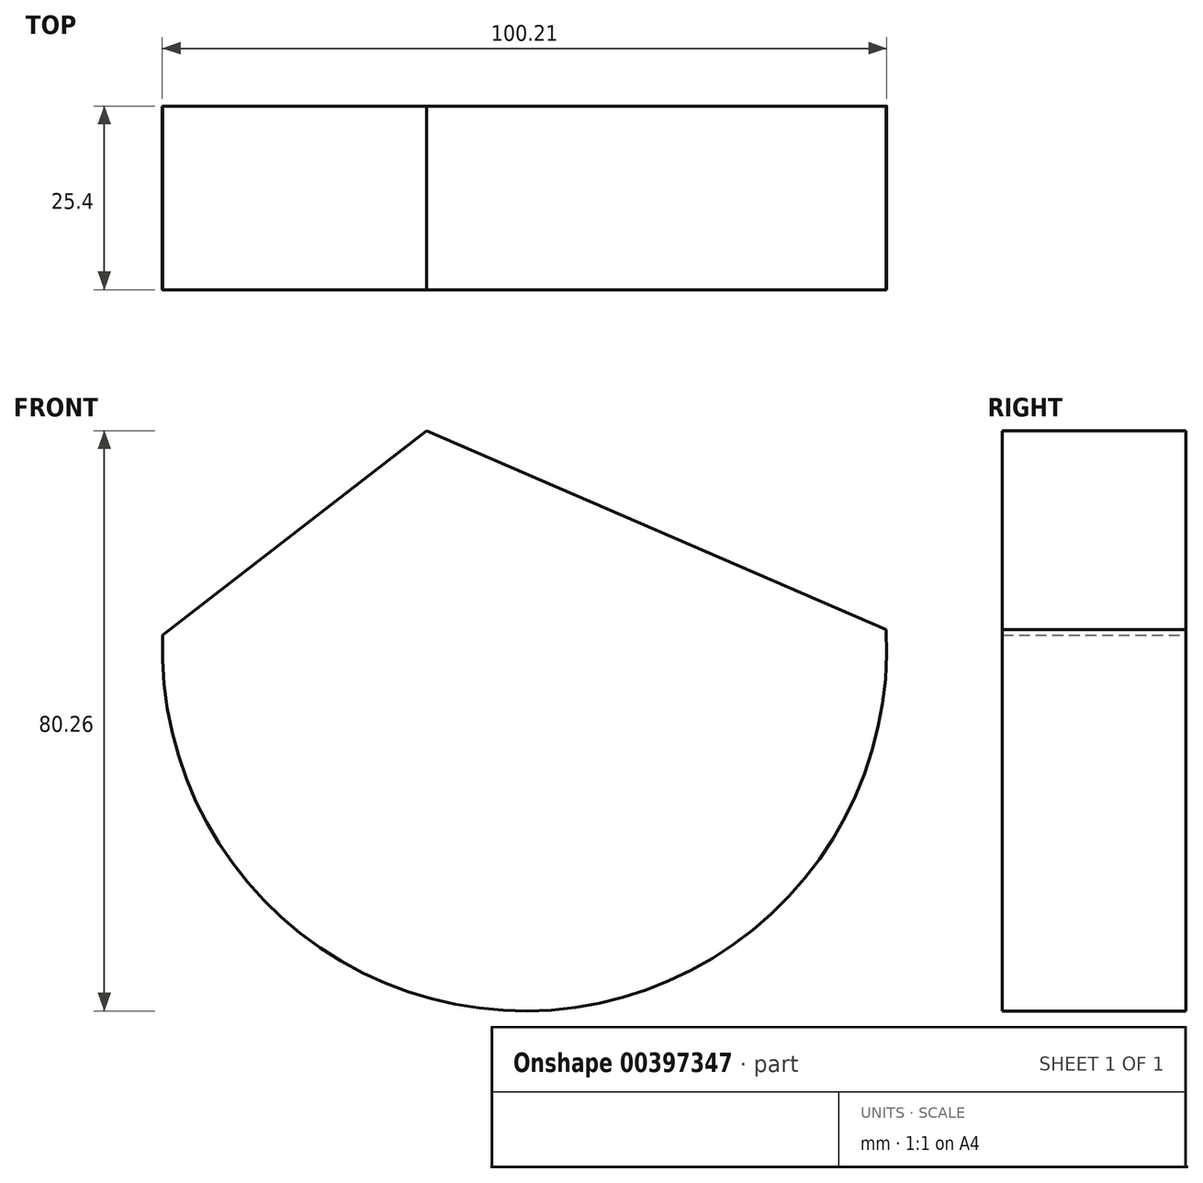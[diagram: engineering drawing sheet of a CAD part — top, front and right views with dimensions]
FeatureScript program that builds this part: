
annotation { "Feature Type Name" : "Feature", "Feature Type Description" : "" }
export const myFeature = defineFeature(function(context is Context, id is Id, definition is map)
    precondition{}
    {
        {
            var Q0;
            Q0=qCreatedBy(makeId("Front.planeOp"),FACE);
            var sketch = newSketch(context, id + "F0", { "sketchPlane" : qUnion([Q0])});
            skLineSegment(sketch, "E0", {"start": v(-58.4, 31.9) * mm, "end": v(-21.9, 60.15) * mm});
            skLineSegment(sketch, "E1", {"start": v(-21.9, 60.15) * mm, "end": v(41.7, 32.63) * mm});
            skArc(sketch, "E2", {"start": v(-58.4, 31.9) * mm, "mid": v(-7.95, -20.11) * mm, "end": v(41.7, 32.63) * mm});
            skSolve(sketch);
        }
        {
            var Q0;
            Q0 = qSketchRegion(id + "F0", true);
            extrude(context, id + "F1", {"entities" : qUnion([Q0]), "depth" : 25.4 * mm});
        }
    });
